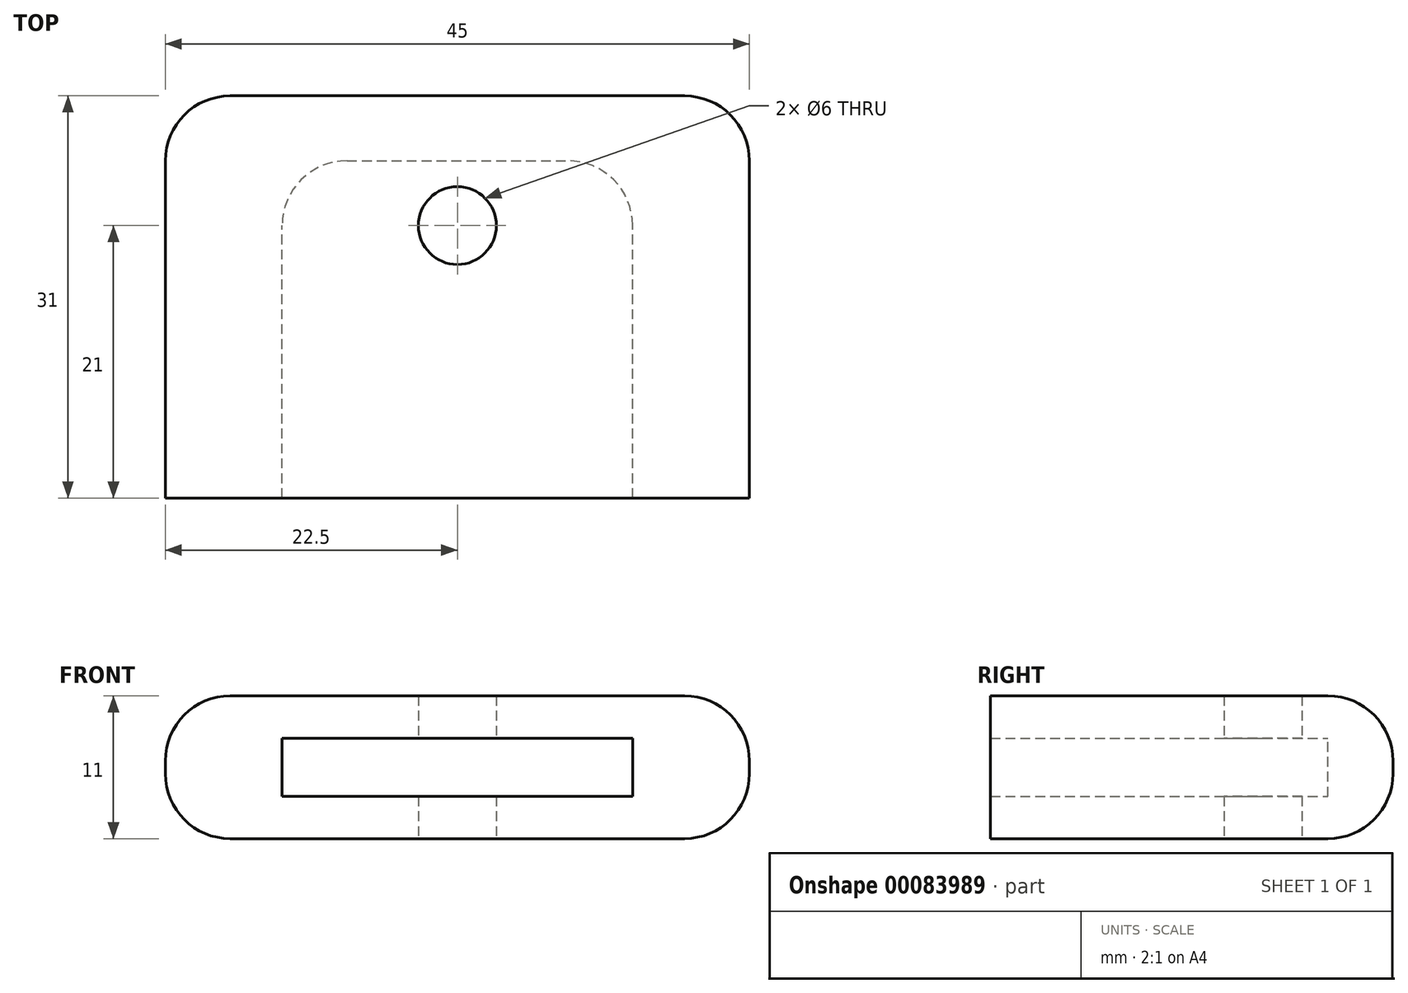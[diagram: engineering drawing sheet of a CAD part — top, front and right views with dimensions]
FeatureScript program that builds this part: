
annotation { "Feature Type Name" : "Feature", "Feature Type Description" : "" }
export const myFeature = defineFeature(function(context is Context, id is Id, definition is map)
    precondition{}
    {
        {
            assignVariable(context, id + "F0", {"name" : "keyThickness", "anyValue" : 4.5});
        }
        {
            var Q0;
            Q0=qCreatedBy(makeId("Top.planeOp"),FACE);
            var sketch = newSketch(context, id + "F1", { "sketchPlane" : qUnion([Q0])});
            skLineSegment(sketch, "E0.bottom", {"start": v(-13.5, -13) * mm, "end": v(13.5, -13) * mm});
            skLineSegment(sketch, "E0.top", {"start": v(-8.5, 13) * mm, "end": v(8.5, 13) * mm});
            skLineSegment(sketch, "E0.left", {"start": v(-13.5, -13) * mm, "end": v(-13.5, 8) * mm});
            skLineSegment(sketch, "E0.right", {"start": v(13.5, -13) * mm, "end": v(13.5, 8) * mm});
            skPoint(sketch, "E0.middle", {"position": v(0, 0) * mm});
            skPoint(sketch, "E1.visualSharp", {"position": v(-13.5, 13) * mm});
            skArc(sketch, "E1.filletArc", {"start": v(-8.5, 13) * mm, "mid": v(-12.04, 11.54) * mm, "end": v(-13.5, 8) * mm});
            skPoint(sketch, "E2.visualSharp", {"position": v(13.5, 13) * mm});
            skArc(sketch, "E2.filletArc", {"start": v(13.5, 8) * mm, "mid": v(12.04, 11.54) * mm, "end": v(8.5, 13) * mm});
            skPoint(sketch, "E3.firstSnap0", {"position": v(0, -13) * mm});
            skLineSegment(sketch, "E3.bottom", {"start": v(-22.5, -13) * mm, "end": v(22.5, -13) * mm});
            skLineSegment(sketch, "E3.top", {"start": v(-17.5, 18) * mm, "end": v(17.5, 18) * mm});
            skLineSegment(sketch, "E3.left", {"start": v(-22.5, -13) * mm, "end": v(-22.5, 13) * mm});
            skLineSegment(sketch, "E3.right", {"start": v(22.5, -13) * mm, "end": v(22.5, 13) * mm});
            skPoint(sketch, "E4.visualSharp", {"position": v(-22.5, 18) * mm});
            skArc(sketch, "E4.filletArc", {"start": v(-17.5, 18) * mm, "mid": v(-21.04, 16.54) * mm, "end": v(-22.5, 13) * mm});
            skPoint(sketch, "E5.visualSharp", {"position": v(22.5, 18) * mm});
            skArc(sketch, "E5.filletArc", {"start": v(22.5, 13) * mm, "mid": v(21.04, 16.54) * mm, "end": v(17.5, 18) * mm});
            skCircle(sketch, "E6", {"center": v(0, 8) * mm, "radius": 3 * mm});
            skSolve(sketch);
        }
        {
            var Q0;
            Q0=makeQuery(id+"F1.imprint","IMPRINT",FACE,{"disambiguationData":[TD([[makeQuery(id+"F1.imprint","IMPRINT",EDGE,{"derivedFrom":sQuery(id+"F1.wireOp",EDGE,"E0.top")}),1.0]])]});
            var Q1;
            Q1=makeQuery(id+"F1.imprint","IMPRINT",FACE,{"disambiguationData":[TD([[makeQuery(id+"F1.imprint","IMPRINT",EDGE,{"derivedFrom":sQuery(id+"F1.wireOp",EDGE,"E0.top")}),-1.0]])]});
            extrude(context, id + "F2", {"entities" : qUnion([Q0, Q1]), "endBound" : BoundingType.SYMMETRIC, "depth" : 11 * mm});
        }
        {
            var Q0;
            Q0=makeQuery(id+"F1.imprint","IMPRINT",FACE,{"disambiguationData":[TD([[makeQuery(id+"F1.imprint","IMPRINT",EDGE,{"derivedFrom":sQuery(id+"F1.wireOp",EDGE,"E0.top")}),-1.0]])]});
            extrude(context, id + "F3", {"entities" : qUnion([Q0]), "operationType" : NewBodyOperationType.REMOVE, "endBound" : BoundingType.SYMMETRIC, "oppositeDirection" : true, "depth" : (getVariable(context, 'keyThickness')) * mm});
        }
        {
            var Q0;
            Q0=makeQuery(id+"F2.opExtrude","CAP_EDGE",EDGE,{"disambiguationData":[OSD([sQuery(id+"F1.wireOp",EDGE,"E3.left")])],"isStart":false});
            var Q1;
            Q1=makeQuery(id+"F2.opExtrude","CAP_EDGE",EDGE,{"disambiguationData":[OSD([sQuery(id+"F1.wireOp",EDGE,"E4.filletArc")])],"isStart":false});
            var Q2;
            Q2=makeQuery(id+"F2.opExtrude","CAP_EDGE",EDGE,{"disambiguationData":[OSD([sQuery(id+"F1.wireOp",EDGE,"E3.top")])],"isStart":false});
            var Q3;
            Q3=makeQuery(id+"F2.opExtrude","CAP_EDGE",EDGE,{"disambiguationData":[OSD([sQuery(id+"F1.wireOp",EDGE,"E5.filletArc")])],"isStart":false});
            var Q4;
            Q4=makeQuery(id+"F2.opExtrude","CAP_EDGE",EDGE,{"disambiguationData":[OSD([sQuery(id+"F1.wireOp",EDGE,"E3.right")])],"isStart":false});
            var Q5;
            Q5=makeQuery(id+"F2.opExtrude","CAP_EDGE",EDGE,{"disambiguationData":[OSD([sQuery(id+"F1.wireOp",EDGE,"E3.right")])],"isStart":true});
            fillet(context, id + "F4", {"entities" : qUnion([Q0, Q1, Q2, Q3, Q4, Q5]), "radius" : 5 * mm, "tangentPropagation" : true, "allowEdgeOverflow" : false});
        }
    });
